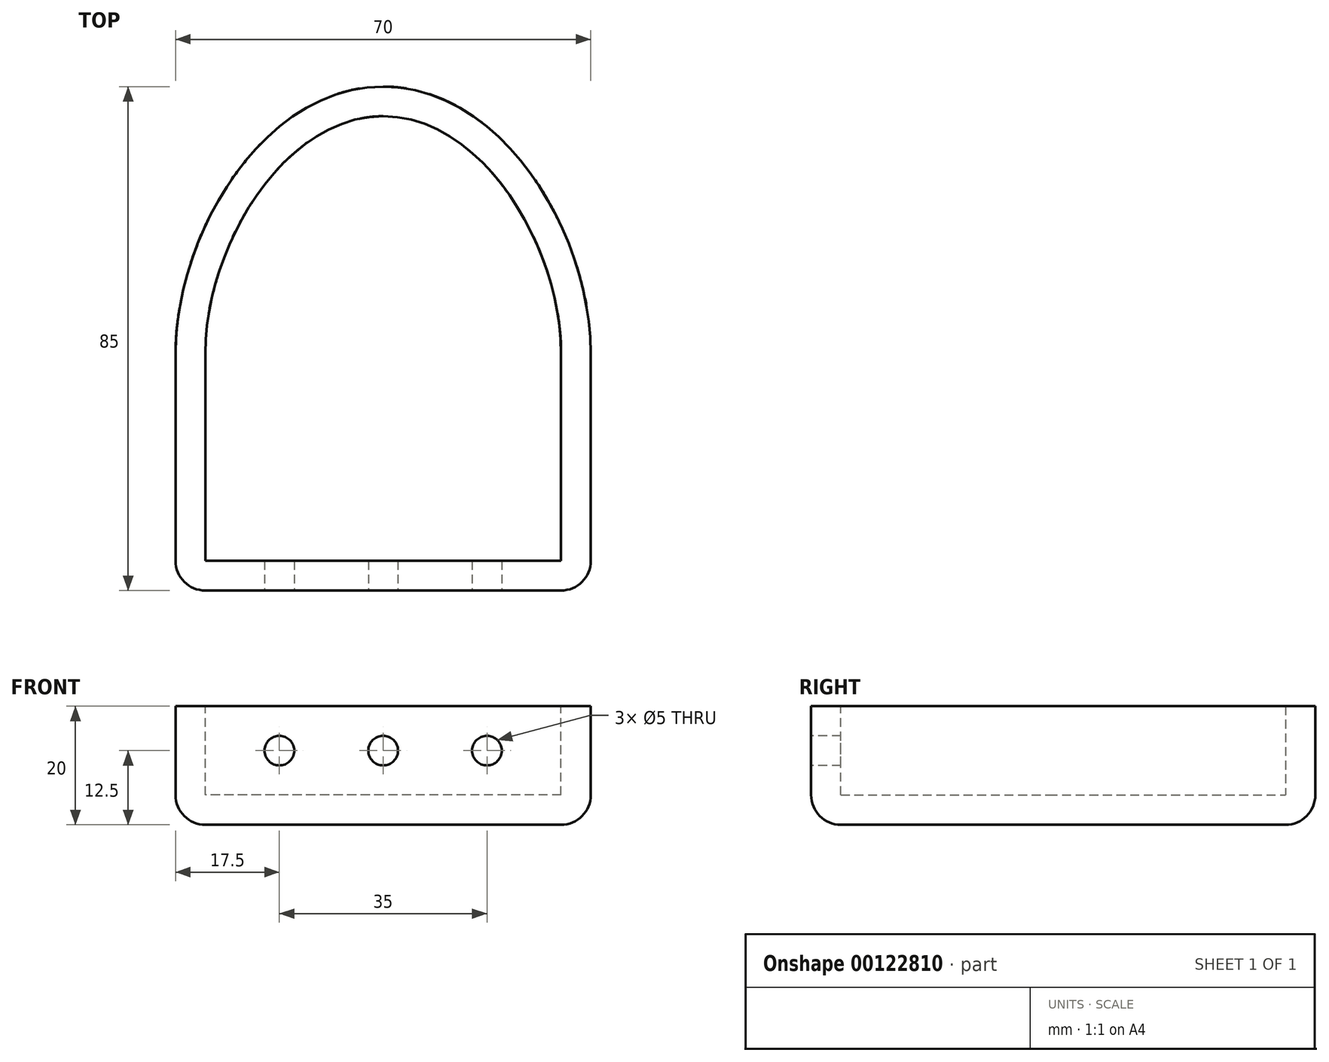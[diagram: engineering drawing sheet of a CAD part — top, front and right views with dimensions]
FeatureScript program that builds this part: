
annotation { "Feature Type Name" : "Feature", "Feature Type Description" : "" }
export const myFeature = defineFeature(function(context is Context, id is Id, definition is map)
    precondition{}
    {
        {
            var Q0;
            Q0=qCreatedBy(makeId("Top.planeOp"),FACE);
            var sketch = newSketch(context, id + "F0", { "sketchPlane" : qUnion([Q0])});
            skLineSegment(sketch, "E0.top", {"start": v(-35, -40) * mm, "end": v(35, -40) * mm});
            skPoint(sketch, "E0.middle", {"position": v(0, 0) * mm});
            skPoint(sketch, "E1.visualSharp", {"position": v(-35, -40) * mm});
            skPoint(sketch, "E2.visualSharp", {"position": v(35, -40) * mm});
            skPoint(sketch, "E3", {"position": v(-35, 0) * mm});
            skPoint(sketch, "E4", {"position": v(35, 0) * mm});
            skLineSegment(sketch, "E5", {"start": v(-35, 0) * mm, "end": v(-35, -40) * mm});
            skLineSegment(sketch, "E6", {"start": v(35, 0) * mm, "end": v(35, -40) * mm});
            skFitSpline(sketch, "E7", {"points": [v(0, 45) * mm, v(-35, 0) * mm], "startDerivative": vector(-60.6, 0) * mm, "endDerivative": vector(0, -60.15) * mm});
            skFitSpline(sketch, "E8.MirrorCS", {"points": [v(0, 45) * mm, v(35, 0) * mm], "startDerivative": vector(60.6, 0) * mm, "endDerivative": vector(0, -60.15) * mm});
            skSolve(sketch);
        }
        {
            var Q0;
            Q0=qSketchRegion(id+"F0",true);
            extrude(context, id + "F1", {"entities" : qUnion([Q0]), "endBound" : BoundingType.SYMMETRIC, "depth" : 25 * mm});
        }
        {
            var Q0;
            Q0=qCreatedBy(makeId("Right.planeOp"),FACE);
            var sketch = newSketch(context, id + "F2", { "sketchPlane" : qUnion([Q0])});
            skLineSegment(sketch, "E9", {"start": v(0, 0) * mm, "end": v(-30, 0) * mm});
            skPoint(sketch, "E10", {"position": v(-30, 0) * mm});
            skLineSegment(sketch, "E11", {"start": v(-30, 12.5) * mm, "end": v(-30, -12.5) * mm});
            skLineSegment(sketch, "E12", {"start": v(-30, -12.5) * mm, "end": v(0, -12.5) * mm});
            skLineSegment(sketch, "E13", {"start": v(-30, 12.5) * mm, "end": v(-15.57, -12.5) * mm});
            skLineSegment(sketch, "E14", {"start": v(-30, 7.5) * mm, "end": v(-27.11, 7.5) * mm});
            skLineSegment(sketch, "E15.bottom", {"start": v(-30, 7.5) * mm, "end": v(-40, 7.5) * mm});
            skLineSegment(sketch, "E15.top", {"start": v(-30, -12.5) * mm, "end": v(-40, -12.5) * mm});
            skLineSegment(sketch, "E15.left", {"start": v(-30, 7.5) * mm, "end": v(-30, -12.5) * mm});
            skLineSegment(sketch, "E15.right", {"start": v(-40, 7.5) * mm, "end": v(-40, -12.5) * mm});
            skSolve(sketch);
        }
        {
            var Q0;
            Q0=makeQuery(id+"F1.opExtrude","CAP_FACE",FACE,{"disambiguationData":[OSD([sQuery(id+"F0.wireOp",EDGE,"E0.top"),sQuery(id+"F0.wireOp",EDGE,"49a04736-c9a8-4021-8eca-e335ee950ef4"),sQuery(id+"F0.wireOp",EDGE,"5cda4a63-8e27-4d9c-be18-28a9360ed2950.MirrorCS"),sQuery(id+"F0.wireOp",EDGE,"E5"),sQuery(id+"F0.wireOp",EDGE,"E6")])],"isStart":true});
            var sketch = newSketch(context, id + "F3", { "sketchPlane" : qUnion([Q0])});
            skLineSegment(sketch, "E16.bottom", {"start": v(35, 40) * mm, "end": v(-25, 40) * mm});
            skLineSegment(sketch, "E16.top", {"start": v(35, 55.57) * mm, "end": v(-25, 55.57) * mm});
            skLineSegment(sketch, "E16.left", {"start": v(35, 40) * mm, "end": v(35, 55.57) * mm});
            skLineSegment(sketch, "E16.right", {"start": v(-25, 40) * mm, "end": v(-25, 55.57) * mm});
            skFitSpline(sketch, "E17", {"points": [v(0, -40) * mm, v(30, 0) * mm], "startDerivative": vector(49.89, 0) * mm, "endDerivative": vector(0, 60.15) * mm});
            skFitSpline(sketch, "E18.MirrorCS", {"points": [v(0, -40) * mm, v(-30, 0) * mm], "startDerivative": vector(-49.89, 0) * mm, "endDerivative": vector(0, 60.15) * mm});
            skFitSpline(sketch, "E19.0", {"points": [v(0, -32) * mm, v(0.64, -32) * mm, v(1.9, -31.9) * mm, v(3.77, -31.49) * mm, v(5.66, -30.78) * mm, v(8.18, -29.45) * mm, v(11.32, -27.03) * mm, v(14.84, -22.99) * mm, v(17.86, -18) * mm, v(20.18, -12.32) * mm, v(21.66, -6.22) * mm, v(22, -2.06) * mm, v(22, 0) * mm]});
            skFitSpline(sketch, "E19.1", {"points": [v(0, -32) * mm, v(-0.64, -32) * mm, v(-1.9, -31.9) * mm, v(-3.77, -31.49) * mm, v(-5.66, -30.78) * mm, v(-8.18, -29.45) * mm, v(-11.32, -27.03) * mm, v(-14.84, -22.99) * mm, v(-17.86, -18) * mm, v(-20.18, -12.32) * mm, v(-21.66, -6.22) * mm, v(-22, -2.06) * mm, v(-22, 0) * mm]});
            skFitSpline(sketch, "E20.0", {"points": [v(0, -27) * mm, v(0.4, -27) * mm, v(1.15, -26.94) * mm, v(2.33, -26.68) * mm, v(3.59, -26.21) * mm, v(4.94, -25.5) * mm, v(6.36, -24.53) * mm, v(8.32, -22.85) * mm, v(10.76, -20.06) * mm, v(13.36, -15.76) * mm, v(15.4, -10.78) * mm, v(16.7, -5.42) * mm, v(17, -1.78) * mm, v(17, 0) * mm]});
            skFitSpline(sketch, "E20.1", {"points": [v(0, -27) * mm, v(-0.4, -27) * mm, v(-1.15, -26.94) * mm, v(-2.33, -26.68) * mm, v(-3.59, -26.21) * mm, v(-4.94, -25.5) * mm, v(-6.36, -24.53) * mm, v(-8.32, -22.85) * mm, v(-10.76, -20.06) * mm, v(-13.36, -15.76) * mm, v(-15.4, -10.78) * mm, v(-16.7, -5.42) * mm, v(-17, -1.78) * mm, v(-17, 0) * mm]});
            skLineSegment(sketch, "E21.bottom", {"start": v(-22, 0) * mm, "end": v(22, 0) * mm});
            skLineSegment(sketch, "E21.top", {"start": v(-22, 10) * mm, "end": v(22, 10) * mm});
            skLineSegment(sketch, "E21.left", {"start": v(-22, 0) * mm, "end": v(-22, 10) * mm});
            skLineSegment(sketch, "E21.right", {"start": v(22, 0) * mm, "end": v(22, 10) * mm});
            skLineSegment(sketch, "E22", {"start": v(-20.56, -10.51) * mm, "end": v(-15.34, -10.51) * mm});
            skLineSegment(sketch, "E23.MirrorCS", {"start": v(20.56, -10.51) * mm, "end": v(15.34, -10.51) * mm});
            skLineSegment(sketch, "E24.top", {"start": v(-22, 5) * mm, "end": v(22, 5) * mm});
            skLineSegment(sketch, "E24.left", {"start": v(-22, 10) * mm, "end": v(-22, 5) * mm});
            skLineSegment(sketch, "E24.right", {"start": v(22, 10) * mm, "end": v(22, 5) * mm});
            skSolve(sketch);
        }
        {
            var Q0;
            Q0=makeQuery(id+"F1.opExtrude","CAP_EDGE",EDGE,{"disambiguationData":[OSD([sQuery(id+"F0.wireOp",EDGE,"E5")])],"isStart":true});
            var Q1;
            Q1=makeQuery(id+"F1.opExtrude","CAP_EDGE",EDGE,{"disambiguationData":[OSD([sQuery(id+"F0.wireOp",EDGE,"E7")])],"isStart":true});
            var Q2;
            Q2=makeQuery(id+"F1.opExtrude","CAP_EDGE",EDGE,{"disambiguationData":[OSD([sQuery(id+"F0.wireOp",EDGE,"E0.top")])],"isStart":false});
            var Q3;
            Q3=makeQuery(id+"F1.opExtrude","CAP_EDGE",EDGE,{"disambiguationData":[OSD([sQuery(id+"F0.wireOp",EDGE,"E5")])],"isStart":false});
            var Q4;
            Q4=makeQuery(id+"F1.opExtrude","SWEPT_EDGE",EDGE,{"disambiguationData":[OSD([sQuery(id+"F0.wireOp",EDGE,"E0.top"),sQuery(id+"F0.wireOp",EDGE,"E5")])]});
            var Q5;
            Q5=makeQuery(id+"F1.opExtrude","SWEPT_EDGE",EDGE,{"disambiguationData":[OSD([sQuery(id+"F0.wireOp",EDGE,"E0.top"),sQuery(id+"F0.wireOp",EDGE,"E6")])]});
            var Q6;
            {var subQ0=sQuery(id+"F0.wireOp",EDGE,"E0.top");var subQ1=sQuery(id+"F0.wireOp",EDGE,"E5");Q6=makeQuery(id+"FKo57LURMALH3DB_1.boolean.opBoolean","SPLIT",EDGE,{"disambiguationData":[TD([makeQuery(id+"F1.opExtrude","SWEPT_FACE",FACE,{"disambiguationData":[OSD([subQ1])]})])],"derivedFrom":makeQuery(id+"F1.opExtrude","CAP_EDGE",EDGE,{"disambiguationData":[OSD([subQ0])],"isStart":true})});}
            var Q7;
            {var subQ0=sQuery(id+"F0.wireOp",EDGE,"E0.top");var subQ1=sQuery(id+"F0.wireOp",EDGE,"E6");Q7=makeQuery(id+"FKo57LURMALH3DB_1.boolean.opBoolean","SPLIT",EDGE,{"disambiguationData":[TD([makeQuery(id+"F1.opExtrude","SWEPT_FACE",FACE,{"disambiguationData":[OSD([subQ1])]})])],"derivedFrom":makeQuery(id+"F1.opExtrude","CAP_EDGE",EDGE,{"disambiguationData":[OSD([subQ0])],"isStart":true})});}
            fillet(context, id + "F4", {"entities" : qUnion([Q0, Q1, Q2, Q3, Q4, Q5, Q6, Q7]), "radius" : 5 * mm, "tangentPropagation" : true, "allowEdgeOverflow" : false});
        }
        {
            var Q0;
            Q0=makeQuery(id+"F1.opExtrude","CAP_FACE",FACE,{"disambiguationData":[OSD([sQuery(id+"F0.wireOp",EDGE,"E0.top"),sQuery(id+"F0.wireOp",EDGE,"E5"),sQuery(id+"F0.wireOp",EDGE,"E6"),sQuery(id+"F0.wireOp",EDGE,"E7"),sQuery(id+"F0.wireOp",EDGE,"E8.MirrorCS")])],"isStart":false});
            var sketch = newSketch(context, id + "F5", { "sketchPlane" : qUnion([Q0])});
            skLineSegment(sketch, "E25.bottom", {"start": v(-45.63, 73.42) * mm, "end": v(45.63, 73.42) * mm});
            skLineSegment(sketch, "E25.top", {"start": v(-45.63, -73.42) * mm, "end": v(45.63, -73.42) * mm});
            skLineSegment(sketch, "E25.left", {"start": v(-45.63, 73.42) * mm, "end": v(-45.63, -73.42) * mm});
            skLineSegment(sketch, "E25.right", {"start": v(45.63, 73.42) * mm, "end": v(45.63, -73.42) * mm});
            skPoint(sketch, "E25.middle", {"position": v(0, 0) * mm});
            skSolve(sketch);
        }
        {
            var Q0;
            Q0=qSketchRegion(id+"F5",true);
            extrude(context, id + "F6", {"entities" : qUnion([Q0]), "operationType" : NewBodyOperationType.REMOVE, "oppositeDirection" : true, "depth" : 5 * mm});
        }
        {
            var Q0;
            Q0=makeQuery(id+"F6.boolean.opBoolean","COPY",FACE,{"derivedFrom":makeQuery(id+"F6.opExtrude","CAP_FACE",FACE,{"disambiguationData":[OSD([sQuery(id+"F5.wireOp",EDGE,"E25.bottom"),sQuery(id+"F5.wireOp",EDGE,"E25.top"),sQuery(id+"F5.wireOp",EDGE,"E25.left"),sQuery(id+"F5.wireOp",EDGE,"E25.right")])],"isStart":false})});
            shell(context, id + "F7", {"entities" : qUnion([Q0]), "thickness" : 5 * mm});
        }
        {
            var Q0;
            Q0=makeQuery(id+"F1.opExtrude","SWEPT_FACE",FACE,{"disambiguationData":[OSD([sQuery(id+"F0.wireOp",EDGE,"E0.top")])]});
            var sketch = newSketch(context, id + "F8", { "sketchPlane" : qUnion([Q0])});
            skLineSegment(sketch, "E26.bottom", {"start": v(-30, 7.5) * mm, "end": v(30, 7.5) * mm});
            skLineSegment(sketch, "E26.top", {"start": v(-30, -7.5) * mm, "end": v(30, -7.5) * mm});
            skLineSegment(sketch, "E26.left", {"start": v(-30, 7.5) * mm, "end": v(-30, -7.5) * mm});
            skLineSegment(sketch, "E26.right", {"start": v(30, 7.5) * mm, "end": v(30, -7.5) * mm});
            skPoint(sketch, "E27", {"position": v(0, 0) * mm});
            skPoint(sketch, "E28", {"position": v(-17.5, 0) * mm});
            skPoint(sketch, "E29", {"position": v(17.5, 0) * mm});
            skSolve(sketch);
        }
        {
            var Q0;
            Q0=sQuery(id+"F8.wireOp",VERTEX,"E28");
            var Q1;
            Q1=sQuery(id+"F8.wireOp",VERTEX,"E29");
            var Q2;
            Q2=sQuery(id+"F8.wireOp",VERTEX,"E27");
            var Q3;
            Q3=makeQuery(id+"F1.opExtrude","SWEPT_BODY",BODY,{"disambiguationData":[OSD([sQuery(id+"F0.wireOp",EDGE,"E0.top"),sQuery(id+"F0.wireOp",EDGE,"E5"),sQuery(id+"F0.wireOp",EDGE,"E6"),sQuery(id+"F0.wireOp",EDGE,"E7"),sQuery(id+"F0.wireOp",EDGE,"E8.MirrorCS")])]});
            hole(context, id + "F9", {"style" : HoleStyle.SIMPLE, "endStyle" : HoleEndStyle.BLIND, "holeDiameter" : 5 * mm, "holeDepth" : 5 * mm, "startFromSketch" : true, "locations" : qUnion([Q0, Q1, Q2]), "scope" : qUnion([Q3])});
        }
    });
